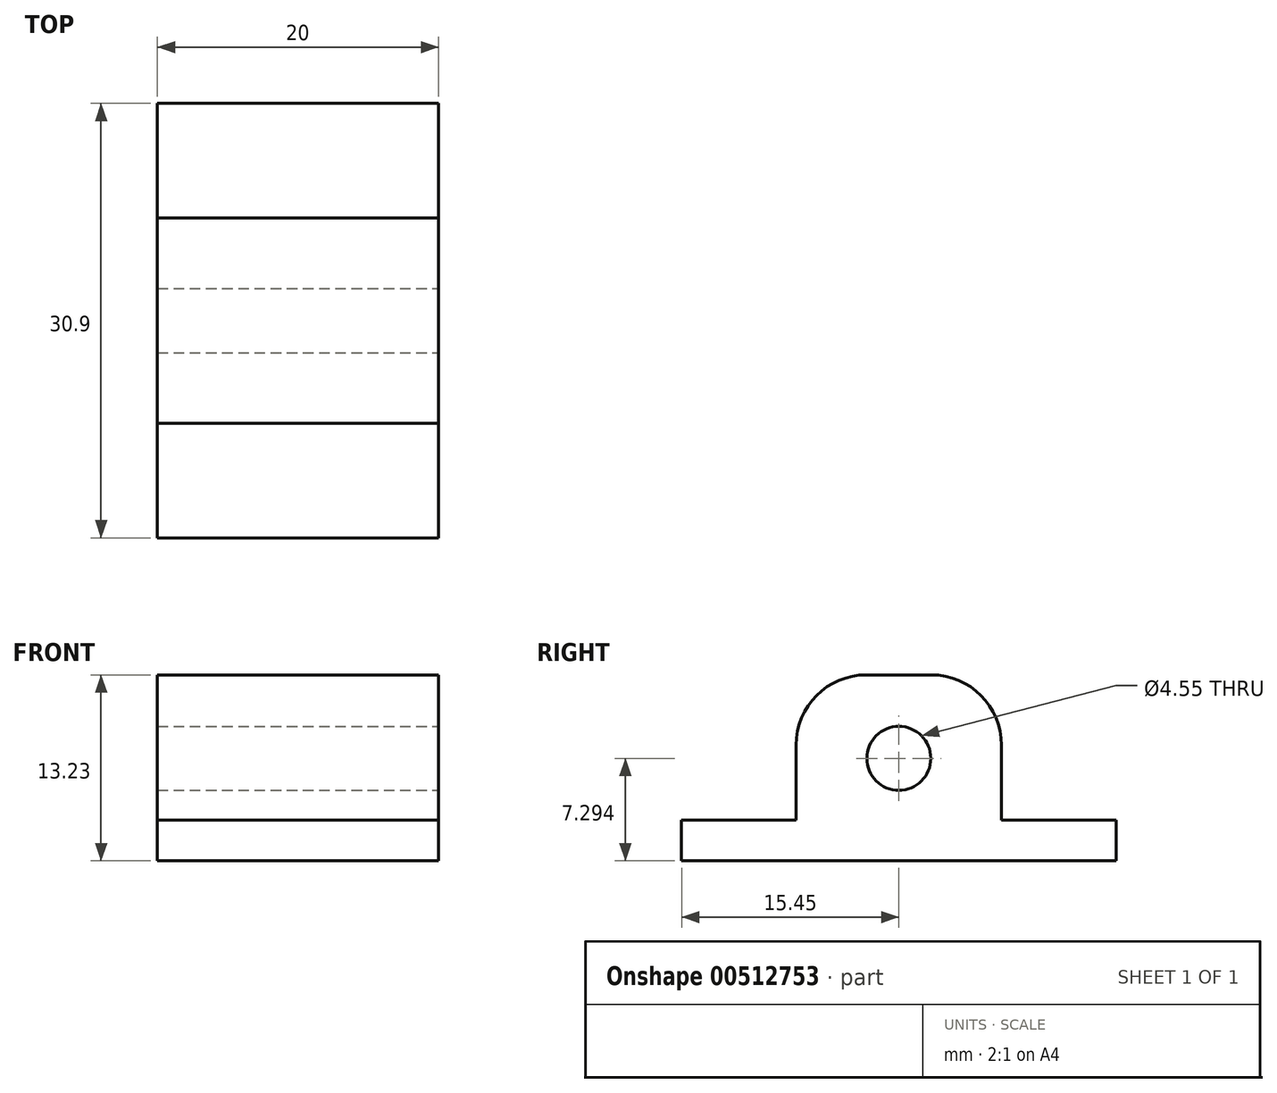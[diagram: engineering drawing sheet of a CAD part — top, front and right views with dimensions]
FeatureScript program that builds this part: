
annotation { "Feature Type Name" : "Feature", "Feature Type Description" : "" }
export const myFeature = defineFeature(function(context is Context, id is Id, definition is map)
    precondition{}
    {
        {
            var Q0;
            Q0=qCreatedBy(makeId("Right.planeOp"),FACE);
            var sketch = newSketch(context, id + "F0", { "sketchPlane" : qUnion([Q0])});
            skLineSegment(sketch, "E0", {"start": v(0, 0) * mm, "end": v(15.45, 0) * mm});
            skLineSegment(sketch, "E1", {"start": v(15.45, 0) * mm, "end": v(15.45, 2.9) * mm});
            skLineSegment(sketch, "E2", {"start": v(15.45, 2.9) * mm, "end": v(7.3, 2.9) * mm});
            skLineSegment(sketch, "E3", {"start": v(7.3, 2.9) * mm, "end": v(7.3, 13.23) * mm});
            skLineSegment(sketch, "E4", {"start": v(7.3, 13.23) * mm, "end": v(0, 13.23) * mm});
            skLineSegment(sketch, "E5", {"start": v(0, 13.23) * mm, "end": v(0, 0) * mm});
            skLineSegment(sketch, "E6.MirrorCS", {"start": v(-7.3, 13.23) * mm, "end": v(0, 13.23) * mm});
            skLineSegment(sketch, "E7.MirrorCS", {"start": v(-7.3, 2.9) * mm, "end": v(-7.3, 13.23) * mm});
            skLineSegment(sketch, "E8.MirrorCS", {"start": v(-15.45, 2.9) * mm, "end": v(-7.3, 2.9) * mm});
            skLineSegment(sketch, "E9.MirrorCS", {"start": v(0, 0) * mm, "end": v(-15.45, 0) * mm});
            skLineSegment(sketch, "E10.MirrorCS", {"start": v(-15.45, 0) * mm, "end": v(-15.45, 2.9) * mm});
            skSolve(sketch);
        }
        {
            var Q0;
            Q0=makeQuery(id+"F0.imprint","IMPRINT",FACE,{"disambiguationData":[TD([[makeQuery(id+"F0.imprint","IMPRINT",EDGE,{"derivedFrom":sQuery(id+"F0.wireOp",EDGE,"E5")}),-1.0]])]});
            var Q1;
            Q1=makeQuery(id+"F0.imprint","IMPRINT",FACE,{"disambiguationData":[TD([[makeQuery(id+"F0.imprint","IMPRINT",EDGE,{"derivedFrom":sQuery(id+"F0.wireOp",EDGE,"E0")}),1.0]])]});
            extrude(context, id + "F1", {"entities" : qUnion([Q0, Q1]), "depth" : 20 * mm, "offsetDistance" : 25 * mm});
        }
        {
            var Q0;
            Q0=makeQuery(id+"F1.opExtrude","CAP_FACE",FACE,{"disambiguationData":[OSD([sQuery(id+"F0.wireOp",EDGE,"E0"),sQuery(id+"F0.wireOp",EDGE,"E1"),sQuery(id+"F0.wireOp",EDGE,"E2"),sQuery(id+"F0.wireOp",EDGE,"E3"),sQuery(id+"F0.wireOp",EDGE,"E4"),sQuery(id+"F0.wireOp",EDGE,"E6.MirrorCS"),sQuery(id+"F0.wireOp",EDGE,"E7.MirrorCS"),sQuery(id+"F0.wireOp",EDGE,"E9.MirrorCS"),sQuery(id+"F0.wireOp",EDGE,"E8.MirrorCS"),sQuery(id+"F0.wireOp",EDGE,"E10.MirrorCS")])],"isStart":false});
            var sketch = newSketch(context, id + "F2", { "sketchPlane" : qUnion([Q0])});
            skCircle(sketch, "E11", {"center": v(0, 7.3) * mm, "radius": 1.88 * mm});
            skSolve(sketch);
        }
        {
            var Q0;
            Q0=sQuery(id+"F2.wireOp",VERTEX,"E11.center");
            var Q1;
            Q1=makeQuery(id+"F1.opExtrude","SWEPT_BODY",BODY,{"disambiguationData":[OSD([sQuery(id+"F0.wireOp",EDGE,"E0"),sQuery(id+"F0.wireOp",EDGE,"E1"),sQuery(id+"F0.wireOp",EDGE,"E2"),sQuery(id+"F0.wireOp",EDGE,"E3"),sQuery(id+"F0.wireOp",EDGE,"E4"),sQuery(id+"F0.wireOp",EDGE,"E6.MirrorCS"),sQuery(id+"F0.wireOp",EDGE,"E7.MirrorCS"),sQuery(id+"F0.wireOp",EDGE,"E9.MirrorCS"),sQuery(id+"F0.wireOp",EDGE,"E8.MirrorCS"),sQuery(id+"F0.wireOp",EDGE,"E10.MirrorCS")])]});
            hole(context, id + "F3", {"style" : HoleStyle.SIMPLE, "endStyle" : HoleEndStyle.THROUGH, "holeDiameter" : 4.55 * mm, "isTappedThrough" : true, "tappedDepth" : 12 * mm, "tapClearance" : 3, "locations" : qUnion([Q0]), "scope" : qUnion([Q1])});
        }
        {
            var Q0;
            Q0=makeQuery(id+"F1.opExtrude","SWEPT_EDGE",EDGE,{"disambiguationData":[OSD([sQuery(id+"F0.wireOp",EDGE,"E3"),sQuery(id+"F0.wireOp",EDGE,"E4")])]});
            var Q1;
            Q1=makeQuery(id+"F1.opExtrude","SWEPT_EDGE",EDGE,{"disambiguationData":[OSD([sQuery(id+"F0.wireOp",EDGE,"E6.MirrorCS"),sQuery(id+"F0.wireOp",EDGE,"E7.MirrorCS")])]});
            fillet(context, id + "F4", {"entities" : qUnion([Q0, Q1]), "radius" : 5 * mm, "tangentPropagation" : true, "allowEdgeOverflow" : false});
        }
    });
